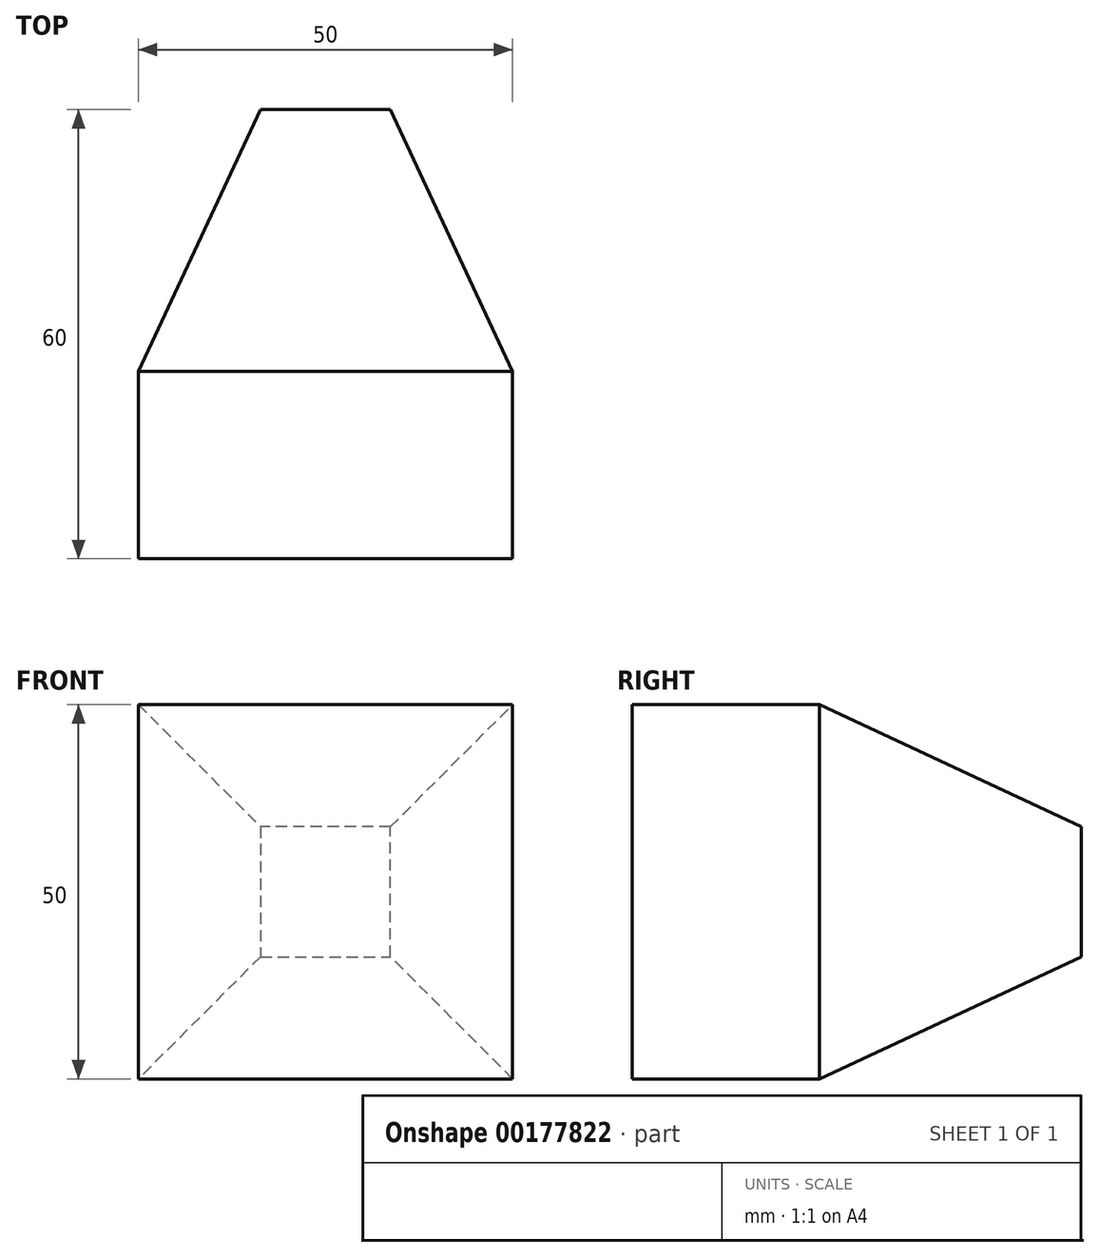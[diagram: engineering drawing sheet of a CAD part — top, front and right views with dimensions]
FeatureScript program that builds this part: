
annotation { "Feature Type Name" : "Feature", "Feature Type Description" : "" }
export const myFeature = defineFeature(function(context is Context, id is Id, definition is map)
    precondition{}
    {
        {
            var Q0;
            Q0=qCreatedBy(makeId("Front.planeOp"),FACE);
            var sketch = newSketch(context, id + "F0", { "sketchPlane" : qUnion([Q0])});
            skLineSegment(sketch, "E0", {"start": v(-43.5, 0) * mm, "end": v(49.55, 0) * mm, "construction": true});
            skLineSegment(sketch, "E1", {"start": v(0, 48.32) * mm, "end": v(0, -48.1) * mm, "construction": true});
            skLineSegment(sketch, "E2.bottom", {"start": v(-25, 25) * mm, "end": v(25, 25) * mm});
            skLineSegment(sketch, "E2.top", {"start": v(-25, -25) * mm, "end": v(25, -25) * mm});
            skLineSegment(sketch, "E2.left", {"start": v(-25, 25) * mm, "end": v(-25, -25) * mm});
            skLineSegment(sketch, "E2.right", {"start": v(25, 25) * mm, "end": v(25, -25) * mm});
            skSolve(sketch);
        }
        {
            var Q0;
            Q0 = qSketchRegion(id + "F0", true);
            extrude(context, id + "F1", {"entities" : qUnion([Q0]), "oppositeDirection" : true, "depth" : 25 * mm});
        }
        {
            var Q0;
            Q0=makeQuery(id+"F1.opExtrude","CAP_FACE",FACE,{"disambiguationData":[OSD([sQuery(id+"F0.wireOp",EDGE,"E2.bottom"),sQuery(id+"F0.wireOp",EDGE,"E2.top"),sQuery(id+"F0.wireOp",EDGE,"E2.left"),sQuery(id+"F0.wireOp",EDGE,"E2.right")])],"isStart":false});
            var sketch = newSketch(context, id + "F2", { "sketchPlane" : qUnion([Q0])});
            skLineSegment(sketch, "E3.0", {"start": v(-25, 25) * mm, "end": v(-25, -25) * mm});
            skLineSegment(sketch, "E3.1", {"start": v(25, 25) * mm, "end": v(-25, 25) * mm});
            skLineSegment(sketch, "E3.2", {"start": v(25, 25) * mm, "end": v(25, -25) * mm});
            skLineSegment(sketch, "E3.3", {"start": v(25, -25) * mm, "end": v(-25, -25) * mm});
            skSolve(sketch);
        }
        {
            var Q0;
            Q0=makeQuery(id+"F2.imprint","IMPRINT",FACE,{"disambiguationData":[TD([[makeQuery(id+"F2.imprint","IMPRINT",EDGE,{"derivedFrom":sQuery(id+"F2.wireOp",EDGE,"E3.0")}),1.0]])]});
            extrude(context, id + "F3", {"entities" : qUnion([Q0]), "operationType" : NewBodyOperationType.ADD, "depth" : 35 * mm, "hasDraft" : true, "draftAngle" : 25 * degree, "draftPullDirection" : true});
        }
    });
